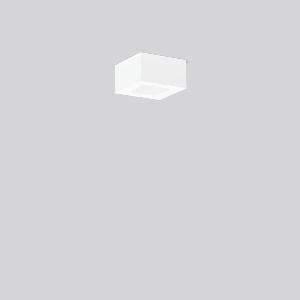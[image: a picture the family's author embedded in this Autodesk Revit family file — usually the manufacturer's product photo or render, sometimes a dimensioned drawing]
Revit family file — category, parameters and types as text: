
# Revit family: toledo_flat_square_a_672259_002_bb42
name_source: partatom
category: Lighting Fixtures
units: mm (PartAtom-declared; Revit-internal decimal feet)

## family parameters
Cut with Voids When Loaded = No
Host = Face
Light Source = No
Part Type = Normal
Room Calculation Point = No
Round Connector Dimension = Use Diameter
Shared = No

## types (1)
- TOLEDO FLAT square A (1 x LED Modul 830, 410 lm, 3000)
    Apparent Load = 6 VA
    CIE Flux Codes = 48 80 96 100 100
    Color Rendering = 80
    Color Temperature = 3000
    Default Elevation = 1800 mm
    Description = Series: TOLEDO FLAT square
Ultra thin surface mounted downlight. For escape route illumination. Surface mounted housing: sheet steel, powder-coated. Square cover plate: die-cast aluminium, powder coated. Light guide and diffuser made of non-yellowing PMMA, opal matt. Driver integrated. Suitable for connection to central battery systems. 
Colour: white
Length: 110 mm
Width: 110 mm
Height: 58 mm
Weight: 560 g
Operating mode: maintained power mode
Lamp: LED
Socket: without socket
Colour temperature: 3000K
Colour rendering index (CRI): 80
System power: 6 W
Rated luminous flux: 410 lm
Luminous flux, emergency: 410 lm
System power, emergency: 6 W
Control gear: Regulated power supply
Protection class: I
Type of protection: IP 40
    Height = 58 mm
    Lamp = 1 x LED Modul 830
    Lamp Light Flux = 410 lm
    Lamp count = 1
    Length = 110 mm
    Lifetime = 50000 h
    Luminous efficacy = 68 lm/W
    Manufacturer = RZB
    ModVariant = No
    Model = 672259.002
    Mounting Place = Ceiling
    Mounting Type = Surface mounted
    Number of Poles = 1
    OnlyDefault = Yes
    Power Factor = 1
    Product Name = TOLEDO FLAT square A
    Product group = Surface mounted downlights
    ProductGroupID = 302
    Protection Class = Protection class I
    Protection Degree = IP 40
    RLX_Detail_Level = 1
    RLX_Emergency_Light_Flux = 410 lm
    RLX_Emergency_Type = 3
    RLX_Emergency_Type_DB = Yes
    RlxData = <blob elided: 8585 chars, md5=95cc907b>
    Socket = socket
    Standby Power = 0 W
    System Light Flux = 410 lm
    System Power = 6 W
    Type Comments = Product without accessories
    Type Image = 901551.002.jpg
    URL = http://relux.com
    VarID = ---
    Voltage = 230 V
    Voltage Range = 220-240 V
    Weight = 0.00 kg
    Width = 110 mm

## geometry (parser evidence)
native form markers: Blend x4, Sweep x10
no freeform markers — native parametric forms only
